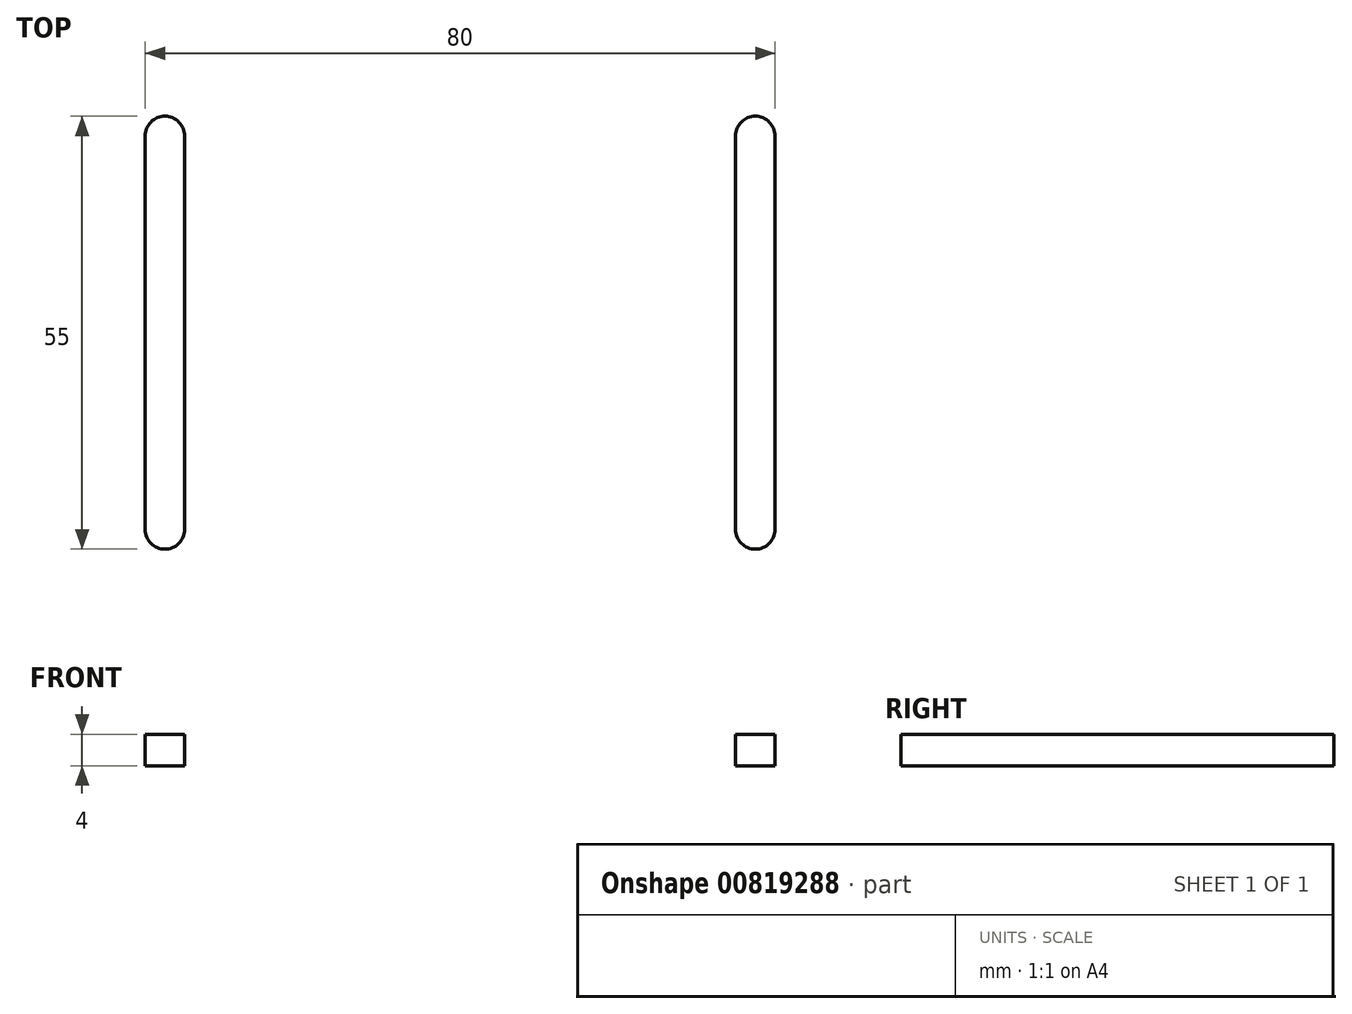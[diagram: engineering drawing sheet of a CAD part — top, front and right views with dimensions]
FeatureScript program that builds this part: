
annotation { "Feature Type Name" : "Feature", "Feature Type Description" : "" }
export const myFeature = defineFeature(function(context is Context, id is Id, definition is map)
    precondition{}
    {
        {
            var Q0;
            Q0=qCreatedBy(makeId("Top.planeOp"),FACE);
            var sketch = newSketch(context, id + "F0", { "sketchPlane" : qUnion([Q0])});
            skLineSegment(sketch, "E0.bottom", {"start": v(0, 0) * mm, "end": v(45, 0) * mm});
            skLineSegment(sketch, "E0.top", {"start": v(0, 140) * mm, "end": v(45, 140) * mm});
            skLineSegment(sketch, "E0.left", {"start": v(0, 0) * mm, "end": v(0, 140) * mm});
            skLineSegment(sketch, "E0.right", {"start": v(45, 0) * mm, "end": v(45, 140) * mm});
            skSolve(sketch);
        }
        {
            var Q0;
            Q0=makeQuery(id+"F0.imprint","IMPRINT",FACE,{"disambiguationData":[TD([[makeQuery(id+"F0.imprint","IMPRINT",EDGE,{"derivedFrom":sQuery(id+"F0.wireOp",EDGE,"E0.bottom")}),1.0]])]});
            extrude(context, id + "F1", {"entities" : qUnion([Q0]), "depth" : 4 * mm, "offsetDistance" : 25 * mm});
        }
        {
            var Q0;
            Q0=makeQuery(id+"F1.opExtrude","SWEPT_EDGE",EDGE,{"disambiguationData":[OSD([sQuery(id+"F0.wireOp",EDGE,"E0.top"),sQuery(id+"F0.wireOp",EDGE,"E0.right")])]});
            fillet(context, id + "F2", {"entities" : qUnion([Q0]), "radius" : 5 * mm, "tangentPropagation" : true, "allowEdgeOverflow" : false});
        }
        {
            var Q0;
            Q0=makeQuery(id+"F1.opExtrude","SWEPT_EDGE",EDGE,{"disambiguationData":[OSD([sQuery(id+"F0.wireOp",EDGE,"E0.bottom"),sQuery(id+"F0.wireOp",EDGE,"E0.right")])]});
            chamfer(context, id + "F3", {"entities" : qUnion([Q0]), "width" : 42.5 * mm, "tangentPropagation" : true});
        }
        {
            var Q0;
            Q0=makeQuery(id+"F1.opExtrude","CAP_FACE",FACE,{"disambiguationData":[OSD([sQuery(id+"F0.wireOp",EDGE,"E0.bottom"),sQuery(id+"F0.wireOp",EDGE,"E0.top"),sQuery(id+"F0.wireOp",EDGE,"E0.left"),sQuery(id+"F0.wireOp",EDGE,"E0.right")])],"isStart":false});
            var sketch = newSketch(context, id + "F4", { "sketchPlane" : qUnion([Q0])});
            skLineSegment(sketch, "E1", {"start": v(15, 83) * mm, "end": v(15, 107) * mm});
            skSolve(sketch);
        }
        {
            var Q0;
            Q0=sQuery(id+"F4.wireOp",VERTEX,"E1.end");
            var Q1;
            Q1=sQuery(id+"F4.wireOp",VERTEX,"E1.start");
            var Q2;
            Q2=makeQuery(id+"F1.opExtrude","SWEPT_BODY",BODY,{"disambiguationData":[OSD([sQuery(id+"F0.wireOp",EDGE,"E0.bottom"),sQuery(id+"F0.wireOp",EDGE,"E0.top"),sQuery(id+"F0.wireOp",EDGE,"E0.left"),sQuery(id+"F0.wireOp",EDGE,"E0.right")])]});
            hole(context, id + "F5", {"style" : HoleStyle.SIMPLE, "endStyle" : HoleEndStyle.THROUGH, "holeDiameter" : 3 * mm, "majorDiameter" : 5 * mm, "isTappedThrough" : true, "tappedDepth" : 12 * mm, "tapClearance" : 3, "locations" : qUnion([Q0, Q1]), "scope" : qUnion([Q2])});
        }
        {
            var Q0;
            Q0=makeQuery(id+"F1.opExtrude","CAP_FACE",FACE,{"disambiguationData":[OSD([sQuery(id+"F0.wireOp",EDGE,"E0.bottom"),sQuery(id+"F0.wireOp",EDGE,"E0.top"),sQuery(id+"F0.wireOp",EDGE,"E0.left"),sQuery(id+"F0.wireOp",EDGE,"E0.right")])],"isStart":false});
            var sketch = newSketch(context, id + "F6", { "sketchPlane" : qUnion([Q0])});
            skLineSegment(sketch, "E2", {"start": v(37.5, 70) * mm, "end": v(37.5, 120) * mm});
            skSolve(sketch);
        }
        {
            var Q0;
            {var subQ1=sQuery(id+"F0.wireOp",EDGE,"E0.left");Q0=makeQuery(id+"F6.imprint","IMPRINT",FACE,{"disambiguationData":[TD([[makeQuery(id+"F6.imprint","IMPRINT",EDGE,{"derivedFrom":makeQuery(id+"F1.opExtrude","CAP_EDGE",EDGE,{"disambiguationData":[OSD([subQ1])],"isStart":false})}),-1.0]])]});}
            var sketch = newSketch(context, id + "F7", { "sketchPlane" : qUnion([Q0])});
            skLineSegment(sketch, "E3.JYB.JYB", {"start": v(37.5, 70) * mm, "end": v(37.5, 120) * mm, "construction": true});
            skArc(sketch, "E3.0.startCap", {"start": v(40, 70) * mm, "mid": v(37.5, 67.5) * mm, "end": v(35, 70) * mm});
            skArc(sketch, "E3.0.endCap", {"start": v(35, 120) * mm, "mid": v(37.5, 122.5) * mm, "end": v(40, 120) * mm});
            skLineSegment(sketch, "E3.0.left", {"start": v(35, 70) * mm, "end": v(35, 120) * mm});
            skLineSegment(sketch, "E3.0.right", {"start": v(40, 70) * mm, "end": v(40, 120) * mm});
            skSolve(sketch);
        }
        {
            var Q0;
            Q0=makeQuery(id+"F7.imprint","IMPRINT",FACE,{"disambiguationData":[TD([[makeQuery(id+"F7.imprint","IMPRINT",EDGE,{"derivedFrom":sQuery(id+"F7.wireOp",EDGE,"E3.0.startCap")}),-1.0]])]});
            extrude(context, id + "F8", {"entities" : qUnion([Q0]), "operationType" : NewBodyOperationType.REMOVE, "oppositeDirection" : true, "depth" : 60.97 * mm, "offsetDistance" : 25 * mm});
        }
        {
            var Q0;
            Q0=makeQuery(id+"F1.opExtrude","SWEPT_BODY",BODY,{"disambiguationData":[OSD([sQuery(id+"F0.wireOp",EDGE,"E0.bottom"),sQuery(id+"F0.wireOp",EDGE,"E0.top"),sQuery(id+"F0.wireOp",EDGE,"E0.left"),sQuery(id+"F0.wireOp",EDGE,"E0.right")])]});
            var Q1;
            Q1=qCreatedBy(makeId("Right.planeOp"),FACE);
            mirror(context, id + "F9", {"operationType" : NewBodyOperationType.ADD, "entities" : qUnion([Q0]), "mirrorPlane" : qUnion([Q1])});
        }
        {
            var Q0;
            {var subQ1=sQuery(id+"F0.wireOp",EDGE,"E0.left");Q0=makeQuery(id+"F6.imprint","IMPRINT",FACE,{"disambiguationData":[TD([[makeQuery(id+"F6.imprint","IMPRINT",EDGE,{"derivedFrom":makeQuery(id+"F1.opExtrude","CAP_EDGE",EDGE,{"disambiguationData":[OSD([subQ1])],"isStart":false})}),-1.0]])]});}
            var sketch = newSketch(context, id + "F10", { "sketchPlane" : qUnion([Q0])});
            skLineSegment(sketch, "E4", {"start": v(-22.26, 130) * mm, "end": v(22.74, 130) * mm});
            skSolve(sketch);
        }
        {
            var Q0;
            Q0=sQuery(id+"F10.wireOp",VERTEX,"E4.start");
            var Q1;
            Q1=sQuery(id+"F10.wireOp",VERTEX,"E4.end");
            var Q2;
            Q2=makeQuery(id+"F1.opExtrude","SWEPT_BODY",BODY,{"disambiguationData":[OSD([sQuery(id+"F0.wireOp",EDGE,"E0.bottom"),sQuery(id+"F0.wireOp",EDGE,"E0.top"),sQuery(id+"F0.wireOp",EDGE,"E0.left"),sQuery(id+"F0.wireOp",EDGE,"E0.right")])]});
            hole(context, id + "F11", {"style" : HoleStyle.SIMPLE, "endStyle" : HoleEndStyle.THROUGH, "holeDiameter" : 3 * mm, "majorDiameter" : 5 * mm, "isTappedThrough" : true, "tappedDepth" : 12 * mm, "tapClearance" : 3, "locations" : qUnion([Q0, Q1]), "scope" : qUnion([Q2])});
        }
        {
            var Q0;
            {var subQ1=sQuery(id+"F0.wireOp",EDGE,"E0.left");Q0=makeQuery(id+"F6.imprint","IMPRINT",FACE,{"disambiguationData":[TD([[makeQuery(id+"F6.imprint","IMPRINT",EDGE,{"derivedFrom":makeQuery(id+"F1.opExtrude","CAP_EDGE",EDGE,{"disambiguationData":[OSD([subQ1])],"isStart":false})}),-1.0]])]});}
            var sketch = newSketch(context, id + "F12", { "sketchPlane" : qUnion([Q0])});
            skLineSegment(sketch, "E5", {"start": v(-8.56, 18.65) * mm, "end": v(9.44, 18.65) * mm});
            skSolve(sketch);
        }
        {
            var Q0;
            Q0=sQuery(id+"F12.wireOp",VERTEX,"E5.start");
            var Q1;
            Q1=sQuery(id+"F12.wireOp",VERTEX,"E5.end");
            var Q2;
            Q2=makeQuery(id+"F1.opExtrude","SWEPT_BODY",BODY,{"disambiguationData":[OSD([sQuery(id+"F0.wireOp",EDGE,"E0.bottom"),sQuery(id+"F0.wireOp",EDGE,"E0.top"),sQuery(id+"F0.wireOp",EDGE,"E0.left"),sQuery(id+"F0.wireOp",EDGE,"E0.right")])]});
            hole(context, id + "F13", {"style" : HoleStyle.SIMPLE, "endStyle" : HoleEndStyle.THROUGH, "holeDiameter" : 3 * mm, "majorDiameter" : 5 * mm, "isTappedThrough" : true, "tappedDepth" : 12 * mm, "tapClearance" : 3, "locations" : qUnion([Q0, Q1]), "scope" : qUnion([Q2])});
        }
    });
